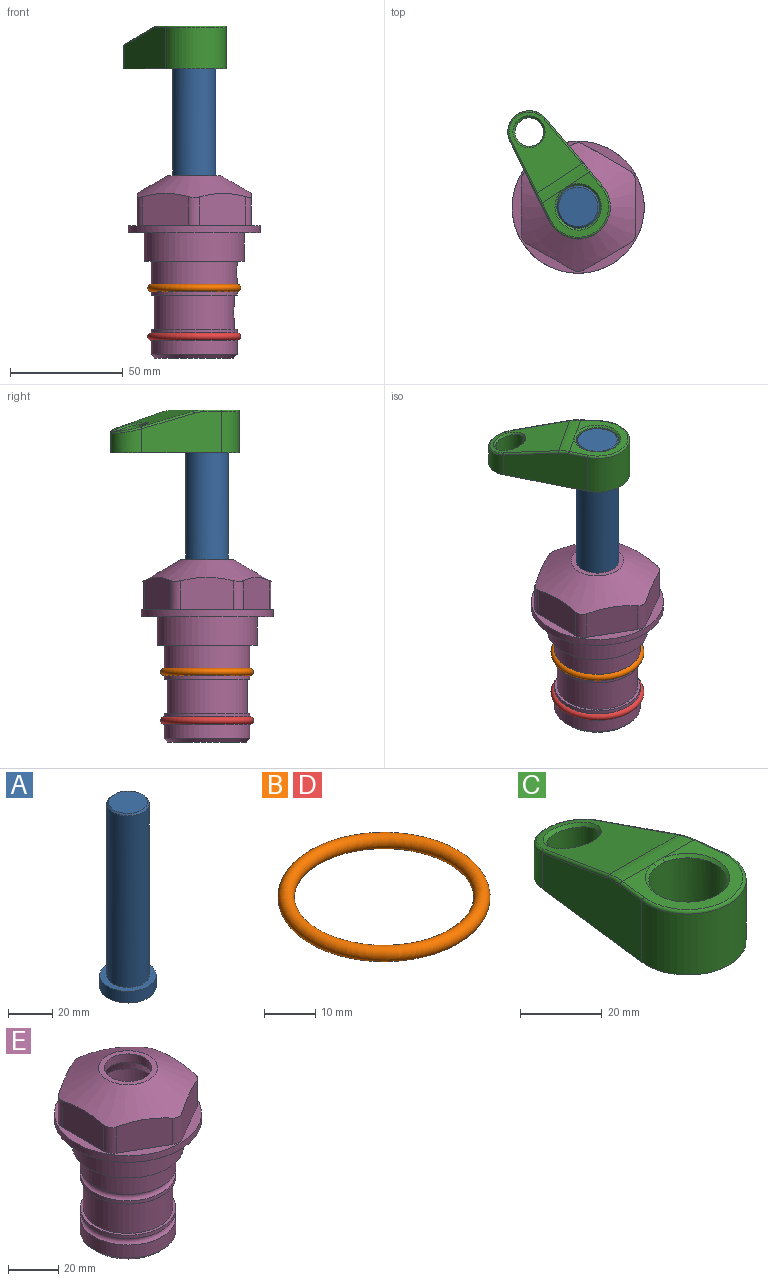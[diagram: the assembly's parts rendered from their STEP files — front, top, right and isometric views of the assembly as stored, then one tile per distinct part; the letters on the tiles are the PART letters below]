
ASSEMBLY  parts=5 mates=4
PART A: 6 faces, bbox 25.4x25.4x101.6 mm
  f0: plane 17.46x17.46mm, normal (0,0,1), area 239.5mm2, adj f5
  f1: plane 25.4x25.4mm, normal (0,0,-1), area 506.7mm2, adj f2
  f2: cylinder r=12.7mm len=25.4mm, axis (0,0,1), area 506.7mm2, adj f1,f3
  f3: plane 25.4x25.4mm, normal (0,0,1), area 221.7mm2, adj f2,f4
  f4: cylinder r=9.53mm len=94.46mm, axis (0,0,1), area 5653mm2, adj f3,f5
  f5: cone r=8.73mm half-angle=45deg, axis (0,0,-1), area 64.4mm2, adj f0,f4
PART B: 1 faces, bbox 44.7x44.7x3.2 mm
  f0: torus R=19.05mm, axis (0,0,1), area 1193.9mm2
PART C: 31 faces, bbox 31.7x65.5x19.8 mm
  f0: plane 39.12x18.26mm, normal (0.99,0.12,0), area 612.2mm2, adj f1,f4,f7,f11,f13,f15
  f1: cylinder r=9.53mm len=18.91mm, axis (0,0,-1), area 296.1mm2, adj f0,f2,f7,f17
  f2: plane 39.12x18.26mm, normal (-0.99,0.12,0), area 612.2mm2, adj f1,f4,f7,f12,f14,f16
  f3: cylinder r=6.35mm len=12.7mm, axis (0,0,-1), area 362.4mm2, adj f7,f18
  f4: cylinder r=14.29mm len=28.58mm, axis (0,0,-1), area 882.2mm2, adj f0,f2,f7,f10
  f5: cylinder r=9.53mm len=19.05mm, axis (0,0,-1), area 1092.6mm2, adj f7,f19,f20
  f6: plane 26.99x23.69mm, normal (0,0,1), area 216.2mm2, adj f9,f10,f11,f12,f19
  f7: plane 63.5x28.58mm, normal (0,0,-1), area 661.8mm2, adj f0,f1,f2,f3,f4,f5,f22,f23
  f8: plane 33.52x23.6mm, normal (0,0.26,0.97), area 486mm2, adj f9,f15,f16,f17,f18
  f9: cylinder r=19.05mm len=24.72mm, axis (1,0,0), area 120.4mm2, adj f6,f8,f13,f14,f20
  f10: torus R=13.49mm, axis (0,0,1), area 59mm2, adj f4,f6,f11,f12
  f11: cylinder r=0.79mm len=8.67mm, axis (0.12,-0.99,0), area 10.8mm2, adj f0,f6,f10,f13
  f12: cylinder r=0.79mm len=8.67mm, axis (0.12,0.99,0), area 10.8mm2, adj f2,f6,f10,f14
  f13: bspline ~4.95x1.42mm, area 6.1mm2, adj f0,f9,f11,f15
  f14: bspline ~4.95x1.42mm, area 6.1mm2, adj f2,f9,f12,f16
  f15: cylinder r=0.79mm len=25.95mm, axis (0.12,-0.96,0.26), area 32.9mm2, adj f0,f8,f13,f17
  f16: cylinder r=0.79mm len=25.95mm, axis (0.12,0.96,-0.26), area 32.9mm2, adj f2,f8,f14,f17
  f17: bspline ~18.91x8.38mm, area 30mm2, adj f1,f8,f15,f16
  f18: bspline ~14.29x14.29mm, area 48.3mm2, adj f3,f8
  f19: cone r=9.53mm half-angle=45deg, axis (0,0,1), area 66.5mm2, adj f5,f6,f20
  f20: bspline ~3.22x0.96mm, area 3.5mm2, adj f5,f9,f19
  f21: plane 2.75x2.72mm, normal (0,0,-1), area 2.9mm2, adj f23,f25,f28
  f22: plane 23.05x15.88mm, normal (-0.99,-0.12,0), area 323.6mm2, adj f7,f25,f26,f27,f28,f29
  f23: plane 23.05x15.88mm, normal (0.99,-0.12,0), area 323.6mm2, adj f7,f21,f25,f27,f28,f30
  f24: cylinder r=9.53mm len=10.69mm, axis (0,0,-1), area 114.7mm2, adj f7,f27,f29,f30
  f25: cylinder r=12.7mm len=20.59mm, axis (0,0,-1), area 381.1mm2, adj f7,f21,f22,f23,f26,f28
  f26: plane 2.75x2.72mm, normal (0,0,-1), area 2.9mm2, adj f22,f25,f28
  f27: plane 19.72x18.37mm, normal (0,-0.26,-0.97), area 291.8mm2, adj f22,f23,f24,f28,f29,f30
  f28: cylinder r=15.88mm len=19.92mm, axis (1,0,0), area 54.8mm2, adj f21,f22,f23,f25,f26,f27
  f29: cylinder r=1.59mm len=11mm, axis (0,0,-1), area 34.7mm2, adj f7,f22,f24,f27
  f30: cylinder r=1.59mm len=11mm, axis (0,0,-1), area 34.7mm2, adj f7,f23,f24,f27
PART D: same geometry as B
PART E: 36 faces, bbox 58.7x58.7x81 mm
  f0: cylinder r=17.78mm len=35.56mm, axis (0,0,1), area 1670.8mm2, adj f23,f24,f31
  f1: cylinder r=19.05mm len=38.1mm, axis (0,0,1), area 1191.9mm2, adj f26,f27,f30
  f2: plane 58.66x58.66mm, normal (0,0,-1), area 1150.6mm2, adj f3,f28
  f3: cylinder r=29.33mm len=58.66mm, axis (0,0,-1), area 585.1mm2, adj f2,f4
  f4: plane 58.66x58.66mm, normal (0,0,1), area 475.9mm2, adj f3,f5,f6,f7,f8,f9,f10,f11
  f5: plane 20.32x14.34mm, normal (-0.5,0.87,0), area 324.4mm2, adj f4,f15,f16,f17
  f6: plane 20.32x14.34mm, normal (0.5,0.87,0), area 324.4mm2, adj f4,f14,f15,f17
  f7: plane 23.48x14.34mm, normal (1,0,0), area 324.4mm2, adj f4,f13,f14,f17
  f8: plane 20.32x14.34mm, normal (0.5,-0.87,0), area 324.4mm2, adj f4,f12,f13,f17
  f9: plane 20.32x14.34mm, normal (-0.5,-0.87,0), area 324.4mm2, adj f4,f11,f12,f17
  f10: plane 23.48x14.34mm, normal (-1,0,0), area 324.4mm2, adj f4,f11,f16,f17
  f11: cylinder r=5.08mm len=12.85mm, axis (0,0,-1), area 67.2mm2, adj f4,f9,f10,f17
  f12: cylinder r=5.08mm len=12.85mm, axis (0,0,-1), area 67.2mm2, adj f4,f8,f9,f17
  f13: cylinder r=5.08mm len=12.85mm, axis (0,0,-1), area 67.2mm2, adj f4,f7,f8,f17
  f14: cylinder r=5.08mm len=12.85mm, axis (0,0,-1), area 67.2mm2, adj f4,f6,f7,f17
  f15: cylinder r=5.08mm len=12.85mm, axis (0,0,-1), area 67.2mm2, adj f4,f5,f6,f17
  f16: cylinder r=5.08mm len=12.85mm, axis (0,0,-1), area 67.2mm2, adj f4,f5,f10,f17
  f17: cone r=11.73mm half-angle=60deg, axis (0,0,-1), area 2071.8mm2, adj f5,f6,f7,f8,f9,f10,f11,f12
  f18: plane 23.46x23.46mm, normal (0,0,1), area 147.4mm2, adj f17,f35
  f19: plane 34.93x34.93mm, normal (0,0,-1), area 958mm2, adj f29
  f20: cylinder r=19.05mm len=38.1mm, axis (0,0,1), area 760.1mm2, adj f21,f29
  f21: torus R=19.05mm, axis (0,0,1), area 565.3mm2, adj f20,f22
  f22: cylinder r=19.05mm len=38.1mm, axis (0,0,1), area 190mm2, adj f21,f23
  f23: plane 38.1x38.1mm, normal (0,0,1), area 146.9mm2, adj f0,f22
  f24: plane 38.1x38.1mm, normal (0,0,-1), area 146.9mm2, adj f0,f25
  f25: cylinder r=19.05mm len=38.1mm, axis (0,0,1), area 190mm2, adj f24,f26
  f26: torus R=19.05mm, axis (0,0,1), area 565.3mm2, adj f1,f25
  f27: plane 44.45x44.45mm, normal (0,0,-1), area 411.7mm2, adj f1,f28
  f28: cylinder r=22.23mm len=44.45mm, axis (0,0,1), area 1773.5mm2, adj f2,f27
  f29: cone r=19.05mm half-angle=45deg, axis (0,0,1), area 257.5mm2, adj f19,f20
  f30: cylinder r=3.17mm len=6.75mm, axis (-1,0,0), area 128mm2, adj f1,f33
  f31: cylinder r=3.17mm len=6.35mm, axis (-1,0,0), area 102.5mm2, adj f0,f33
  f32: plane 25.4x25.4mm, normal (0,0,1), area 506.7mm2, adj f33
  f33: cylinder r=12.7mm len=66.42mm, axis (0,0,-1), area 5236.2mm2, adj f30,f31,f32,f34
  f34: cone r=9.53mm half-angle=30deg, axis (0,0,-1), area 443.4mm2, adj f33,f35
  f35: cylinder r=9.53mm len=19.05mm, axis (0,0,-1), area 240.9mm2, adj f18,f34
PLACE A rot(axis=(0,0,1),33.2deg) t=(0,0,27.55)mm
PLACE B at identity
PLACE C rot(axis=(0,0,1),33.2deg) t=(0,0,28.35)mm
PLACE D t=(0,0,-21.59)mm
PLACE E at identity fixed
MATE fastened C.f4 <-> A.f2  axis (0,0,-1) through (0,0,91.05)mm
MATE cylindrical E.f0 <-> A.f2  axis (0,0,1) through (0,0,-50.55)mm
MATE fastened B.f0 <-> E.f0  axis (0,0,1) through (0,0,-24.51)mm
MATE fastened D.f0 <-> E.f0  axis (0,0,1) through (0,0,-46.1)mm
